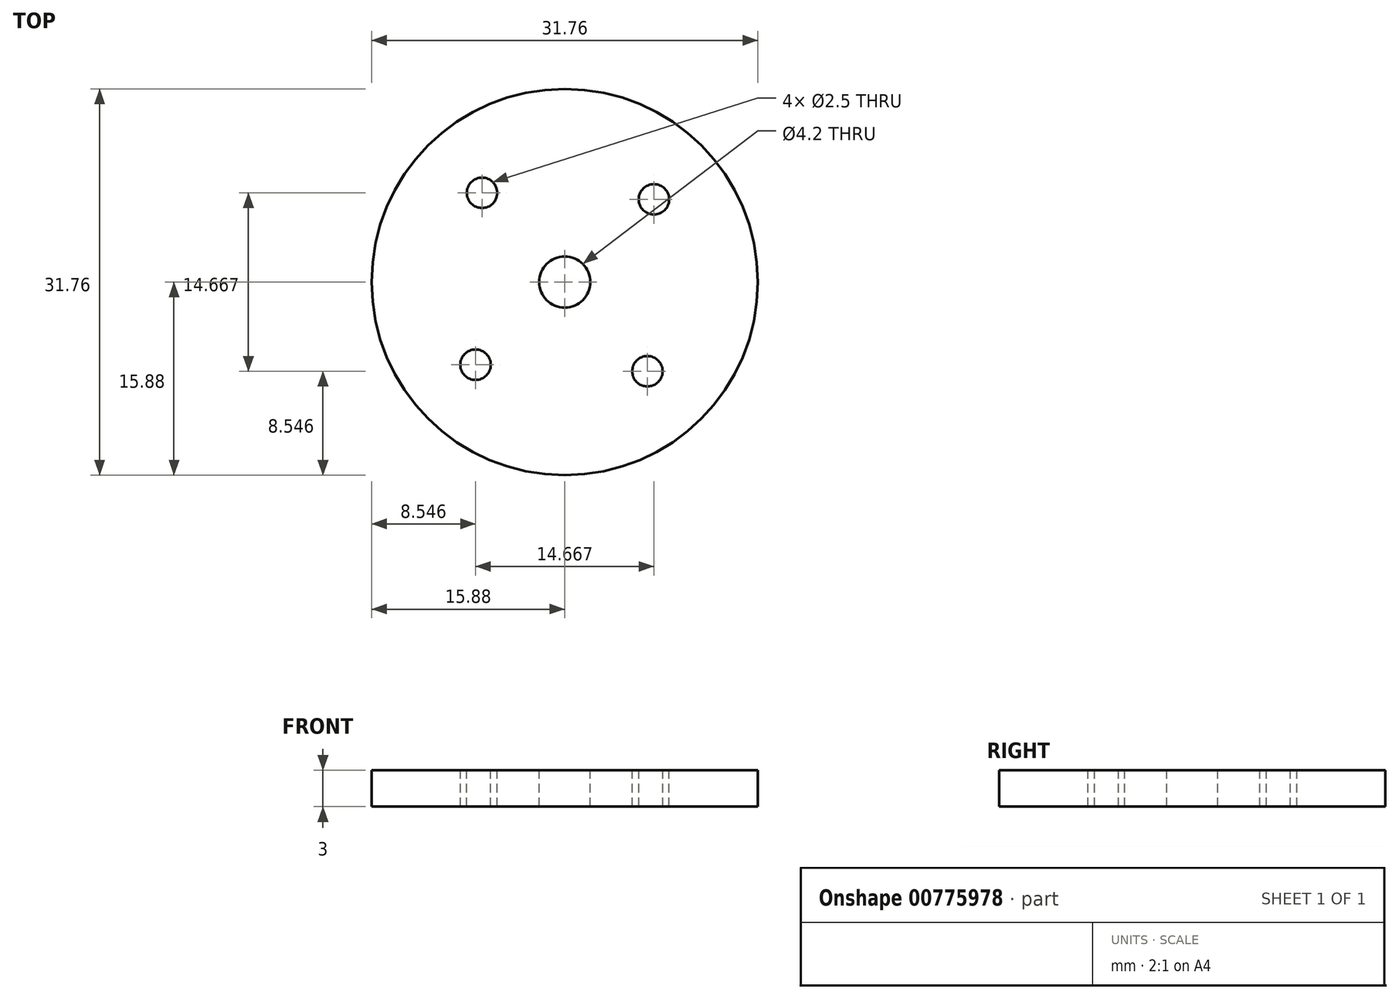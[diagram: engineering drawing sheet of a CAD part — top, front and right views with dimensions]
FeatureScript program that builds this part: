
annotation { "Feature Type Name" : "Feature", "Feature Type Description" : "" }
export const myFeature = defineFeature(function(context is Context, id is Id, definition is map)
    precondition{}
    {
        {
            var Q0;
            Q0=qCreatedBy(makeId("Top.planeOp"),FACE);
            var sketch = newSketch(context, id + "F0", { "sketchPlane" : qUnion([Q0])});
            skCircle(sketch, "E0", {"center": v(0, 0) * mm, "radius": 15.88 * mm});
            skSolve(sketch);
        }
        {
            var Q0;
            Q0=qSketchRegion(id+"F0",true);
            extrude(context, id + "F1", {"entities" : qUnion([Q0]), "depth" : 3 * mm, "offsetDistance" : 25.4 * mm});
        }
        {
            var Q0;
            Q0=makeQuery(id+"F1.opExtrude","CAP_FACE",FACE,{"disambiguationData":[OSD([sQuery(id+"F0.wireOp",EDGE,"E0")])],"isStart":false});
            var sketch = newSketch(context, id + "F2", { "sketchPlane" : qUnion([Q0])});
            skCircle(sketch, "E1", {"center": v(0, 0) * mm, "radius": 10 * mm, "construction": true});
            skCircle(sketch, "E2", {"center": v(-7.33, -6.8) * mm, "radius": 1.25 * mm});
            skCircle(sketch, "E3.1.0", {"center": v(6.8, -7.33) * mm, "radius": 1.25 * mm});
            skCircle(sketch, "E3.1.1", {"center": v(0, 0) * mm, "radius": 10 * mm});
            skCircle(sketch, "E3.2.0", {"center": v(7.33, 6.8) * mm, "radius": 1.25 * mm});
            skCircle(sketch, "E3.2.1", {"center": v(0, 0) * mm, "radius": 10 * mm});
            skCircle(sketch, "E3.3.0", {"center": v(-6.8, 7.33) * mm, "radius": 1.25 * mm});
            skCircle(sketch, "E3.3.1", {"center": v(0, 0) * mm, "radius": 10 * mm});
            skSolve(sketch);
        }
        {
            var Q0;
            {var subQ0=sQuery(id+"F2.wireOp",EDGE,"E3.3.1");var subQ1=sQuery(id+"F2.wireOp",EDGE,"E3.3.0");var subQ2=makeQuery(id+"F2.imprint","INTERSECT",VERTEX,{"disambiguationData":[OD(0.0)],"derivedFrom":[subQ1,subQ0]});Q0=makeQuery(id+"F2.imprint","IMPRINT",FACE,{"disambiguationData":[TD([[makeQuery(id+"F2.imprint","IMPRINT",EDGE,{"disambiguationData":[TD([[subQ2,-1.0]])],"derivedFrom":subQ1}),1.0]])]});}
            var Q1;
            {var subQ0=sQuery(id+"F2.wireOp",EDGE,"E3.3.1");var subQ1=sQuery(id+"F2.wireOp",EDGE,"E3.3.0");var subQ2=makeQuery(id+"F2.imprint","INTERSECT",VERTEX,{"disambiguationData":[OD(0.0)],"derivedFrom":[subQ1,subQ0]});Q1=makeQuery(id+"F2.imprint","IMPRINT",FACE,{"disambiguationData":[TD([[makeQuery(id+"F2.imprint","IMPRINT",EDGE,{"disambiguationData":[TD([[subQ2,1.0]])],"derivedFrom":subQ1}),1.0]])]});}
            var Q2;
            {var subQ0=sQuery(id+"F2.wireOp",EDGE,"E3.3.1");var subQ1=sQuery(id+"F2.wireOp",EDGE,"E3.2.0");var subQ2=makeQuery(id+"F2.imprint","INTERSECT",VERTEX,{"disambiguationData":[OD(0.0)],"derivedFrom":[subQ1,subQ0]});Q2=makeQuery(id+"F2.imprint","IMPRINT",FACE,{"disambiguationData":[TD([[makeQuery(id+"F2.imprint","IMPRINT",EDGE,{"disambiguationData":[TD([[subQ2,-1.0]])],"derivedFrom":subQ1}),1.0]])]});}
            var Q3;
            {var subQ0=sQuery(id+"F2.wireOp",EDGE,"E3.3.1");var subQ1=sQuery(id+"F2.wireOp",EDGE,"E3.2.0");var subQ2=makeQuery(id+"F2.imprint","INTERSECT",VERTEX,{"disambiguationData":[OD(0.0)],"derivedFrom":[subQ1,subQ0]});Q3=makeQuery(id+"F2.imprint","IMPRINT",FACE,{"disambiguationData":[TD([[makeQuery(id+"F2.imprint","IMPRINT",EDGE,{"disambiguationData":[TD([[subQ2,1.0]])],"derivedFrom":subQ1}),1.0]])]});}
            var Q4;
            {var subQ0=sQuery(id+"F2.wireOp",EDGE,"E3.3.1");var subQ1=sQuery(id+"F2.wireOp",EDGE,"E3.1.0");var subQ2=makeQuery(id+"F2.imprint","INTERSECT",VERTEX,{"disambiguationData":[OD(0.0)],"derivedFrom":[subQ1,subQ0]});Q4=makeQuery(id+"F2.imprint","IMPRINT",FACE,{"disambiguationData":[TD([[makeQuery(id+"F2.imprint","IMPRINT",EDGE,{"disambiguationData":[TD([[subQ2,-1.0]])],"derivedFrom":subQ1}),1.0]])]});}
            var Q5;
            {var subQ0=sQuery(id+"F2.wireOp",EDGE,"E3.3.1");var subQ1=sQuery(id+"F2.wireOp",EDGE,"E3.1.0");var subQ2=makeQuery(id+"F2.imprint","INTERSECT",VERTEX,{"disambiguationData":[OD(0.0)],"derivedFrom":[subQ1,subQ0]});Q5=makeQuery(id+"F2.imprint","IMPRINT",FACE,{"disambiguationData":[TD([[makeQuery(id+"F2.imprint","IMPRINT",EDGE,{"disambiguationData":[TD([[subQ2,1.0]])],"derivedFrom":subQ1}),1.0]])]});}
            var Q6;
            {var subQ0=sQuery(id+"F2.wireOp",EDGE,"E3.3.1");var subQ1=sQuery(id+"F2.wireOp",EDGE,"E2");var subQ2=makeQuery(id+"F2.imprint","INTERSECT",VERTEX,{"disambiguationData":[OD(0.0)],"derivedFrom":[subQ1,subQ0]});Q6=makeQuery(id+"F2.imprint","IMPRINT",FACE,{"disambiguationData":[TD([[makeQuery(id+"F2.imprint","IMPRINT",EDGE,{"disambiguationData":[TD([[subQ2,1.0]])],"derivedFrom":subQ1}),1.0]])]});}
            var Q7;
            {var subQ0=sQuery(id+"F2.wireOp",EDGE,"E3.3.1");var subQ1=sQuery(id+"F2.wireOp",EDGE,"E2");var subQ2=makeQuery(id+"F2.imprint","INTERSECT",VERTEX,{"disambiguationData":[OD(0.0)],"derivedFrom":[subQ1,subQ0]});Q7=makeQuery(id+"F2.imprint","IMPRINT",FACE,{"disambiguationData":[TD([[makeQuery(id+"F2.imprint","IMPRINT",EDGE,{"disambiguationData":[TD([[subQ2,-1.0]])],"derivedFrom":subQ1}),1.0]])]});}
            var Q8;
            Q8=sQuery(id+"F2.wireOp",EDGE,"E1");
            extrude(context, id + "F3", {"entities" : qUnion([Q0, Q1, Q2, Q3, Q4, Q5, Q6, Q7]), "operationType" : NewBodyOperationType.REMOVE, "surfaceEntities" : qUnion([Q8]), "oppositeDirection" : true, "depth" : 5 * mm, "offsetDistance" : 25.4 * mm});
        }
        {
            var Q0;
            Q0=makeQuery(id+"F1.opExtrude","CAP_FACE",FACE,{"disambiguationData":[OSD([sQuery(id+"F0.wireOp",EDGE,"E0")])],"isStart":false});
            var sketch = newSketch(context, id + "F4", { "sketchPlane" : qUnion([Q0])});
            skCircle(sketch, "E4", {"center": v(0, 0) * mm, "radius": 2.1 * mm});
            skSolve(sketch);
        }
        {
            var Q0;
            Q0 = qSketchRegion(id + "F4", true);
            var Q1;
            Q1=makeQuery(id+"F1.opExtrude","CAP_FACE",FACE,{"disambiguationData":[OSD([sQuery(id+"F0.wireOp",EDGE,"E0")])],"isStart":true});
            extrude(context, id + "F5", {"entities" : qUnion([Q0]), "operationType" : NewBodyOperationType.REMOVE, "endBound" : BoundingType.UP_TO_SURFACE, "oppositeDirection" : true, "depth" : 25 * mm, "endBoundEntityFace" : qUnion([Q1]), "offsetDistance" : 25 * mm});
        }
    });
